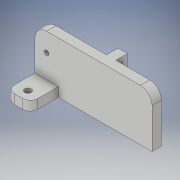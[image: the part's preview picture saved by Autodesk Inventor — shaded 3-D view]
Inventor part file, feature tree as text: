
AUTODESK INVENTOR PART (.ipt)
format: ipt  version: 2018 (Build 220112000, 112)  size: 187,904 bytes
history: native  units: in
note: dims shown in document units (in); Inventor stores cm internally (conversion verified against a paired STEP export)
features: extrude x10, sketch x10, fillet x2
ambient origin geometry x8: Origin, YZ Plane, XZ Plane, XY Plane, X Axis, Y Axis, Z Axis, Center Point
bodies: Solid1 (feature_tree)
feature tree (22):
  extrude  "Extrusion1"  Depth=1.9685in
  fillet  "Fillet1"  Radius=0.7874in
  extrude  "Extrusion2"  Depth=0.1969in TaperAngle=0.0deg
  extrude  "Extrusion3"  Depth=0.1575in
  extrude  "Extrusion9"  Depth=0.4724in TaperAngle=0.0deg
  extrude  "Extrusion10"  Depth=0.4724in TaperAngle=0.0deg
  fillet  "Fillet4"  Radius=0.125in
  extrude  "Extrusion11"  Depth=0.0787in
  extrude  "Extrusion12"  TaperAngle=0.0deg  [1 undecoded]
  extrude  "Extrusion13"  Depth=0.1969in TaperAngle=0.0deg
  extrude  "Extrusion14"  Depth=0.0787in
  extrude  "Extrusion15"  Depth=0.0787in
  sketch  "Sketch1"  dims[d0=0.1575in d1=1.9685in d2=0.7874in d3=0.0in]
  sketch  "Sketch2"  dims[d4=0.1969in d7=0.5906in d8=0.0in]
  sketch  "Sketch3"  dims[d9=0.0787in d10=0.0in d36=0.1575in]
  sketch  "Sketch8"  dims[d37=0.3937in d38=0.4724in d39=0.0in]
  sketch  "Sketch9"  dims[d40=0.1575in d41=0.4724in d42=0.0in d43=0.125in]
  sketch  "Sketch10"  dims[d44=0.4724in d45=0.0787in]
  sketch  "Sketch11"  dims[d46=0.9252in d47=0.0in]
  sketch  "Sketch12"  dims[d48=0.0787in d49=0.1969in d50=0.0in]
  sketch  "Sketch13"  dims[d51=0.1575in d52=0.0787in]
  sketch  "Sketch14"  dims[d53=0.7874in d54=0.0in d57=0.0787in d58=0.0787in d59=0.1181in d60=0.0in d61=0.1575in d62=0.0984in d63=0.0in d64=0.0787in d65=0.0984in d66=0.0in]
note: 1 required parameter value undecoded (feature->parameter linkage not recoverable at this tier; creation-order binding heuristic only, values carry confidence <= 0.55)
